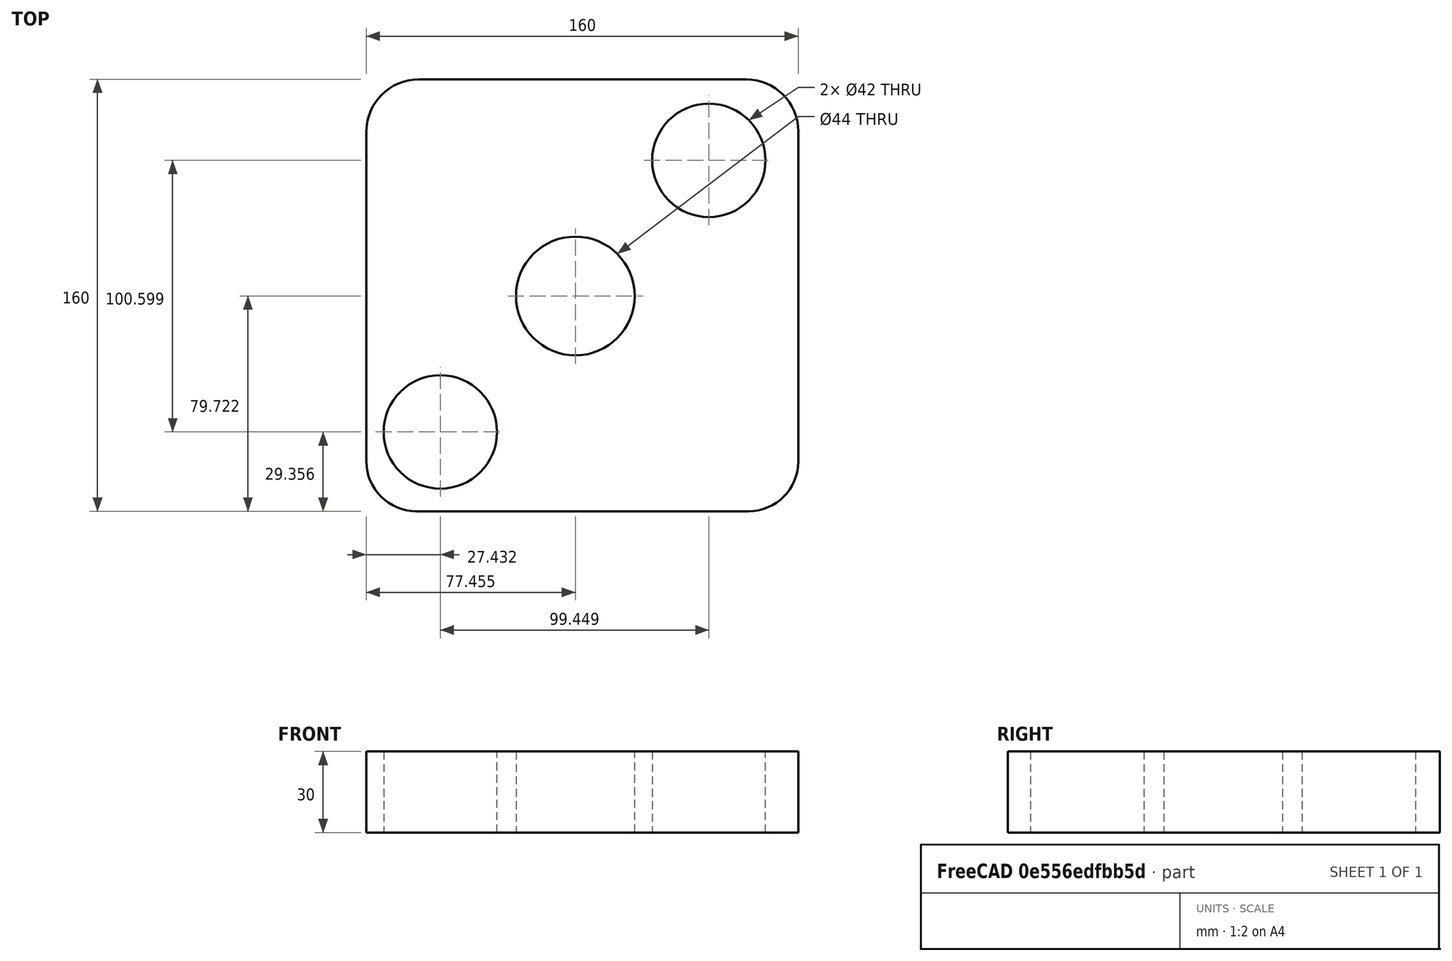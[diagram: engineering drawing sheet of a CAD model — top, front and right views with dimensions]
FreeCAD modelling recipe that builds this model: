
FCSTD DOCUMENT  (FreeCAD 0.18R16131 (Git))
Label: Momentum_Mold_Plate_1-3_160X160
License: All rights reserved
LicenseURL: http://en.wikipedia.org/wiki/All_rights_reserved
objects: Sketcher::SketchObject×1, PartDesign::Pad×1, PartDesign::Body×1
note: 4 computed .brp shape members not serialized (recipe doc carries the construction recipe); baked Part::Feature solids carry a one-line shape summary decoded from their .brp

FEATURE [Sketcher::SketchObject] Sketch
  MapMode = 5
  Support = -> [XY_Plane]
  sketch-geometry (11):
    g0: LineSegment StartX=-58.3579 StartY=-60.0631 StartZ=0 EndX=64.6457 EndY=-60.0631 EndZ=0
    g1: LineSegment StartX=83.0124 StartY=-41.6964 StartZ=0 EndX=83.0124 EndY=80.6112 EndZ=0
    g2: LineSegment StartX=63.6866 StartY=99.9369 StartZ=0 EndX=-57.4704 EndY=99.9369 EndZ=0
    g3: LineSegment StartX=-76.9876 StartY=80.4196 StartZ=0 EndX=-76.9876 EndY=-41.4333 EndZ=0
    g4: ArcOfCircle CenterX=-57.4704 CenterY=80.4196 CenterZ=0 NormalX=0 NormalY=0 NormalZ=1 AngleXU=0 Radius=19.5173 StartAngle=1.5708 EndAngle=3.14159
    g5: ArcOfCircle CenterX=63.6866 CenterY=80.6112 CenterZ=0 NormalX=0 NormalY=0 NormalZ=1 AngleXU=0 Radius=19.3258 StartAngle=0 EndAngle=1.5708
    g6: ArcOfCircle CenterX=64.6457 CenterY=-41.6964 CenterZ=0 NormalX=0 NormalY=0 NormalZ=1 AngleXU=0 Radius=18.3666 StartAngle=4.71239 EndAngle=6.28319
    g7: ArcOfCircle CenterX=-58.3579 CenterY=-41.4333 CenterZ=0 NormalX=0 NormalY=0 NormalZ=1 AngleXU=0 Radius=18.6298 StartAngle=3.14159 EndAngle=4.71239
    g8: Circle CenterX=-49.558 CenterY=-30.7045 CenterZ=0 NormalX=0 NormalY=0 NormalZ=1 AngleXU=0 Radius=21
    g9: Circle CenterX=49.8911 CenterY=69.8944 CenterZ=0 NormalX=0 NormalY=0 NormalZ=1 AngleXU=0 Radius=21
    g10: Circle CenterX=0.465053 CenterY=19.662 CenterZ=0 NormalX=0 NormalY=0 NormalZ=1 AngleXU=0 Radius=22
  constraints (15):
    c: Horizontal(g0)
    c: Horizontal(g2)
    c: Vertical(g1)
    c: Vertical(g3)
    c: Tangent(g2,g4) = -1.5708
    c: Tangent(g3,g4) = -1.5708
    c: Tangent(g2,g5) = -1.5708
    c: Tangent(g1,g5) = -1.5708
    c: Tangent(g1,g6) = -1.5708
    c: Tangent(g0,g6) = -1.5708
    c: Tangent(g0,g7) = -1.5708
    c: Tangent(g3,g7) = -1.5708
    c: Radius(g8) = 21
    c: Radius(g9) = 21
    c: Radius(g10) = 22
FEATURE [PartDesign::Pad] Pad
  Length = 30
  Length2 = 100
  Profile = -> Sketch
  Type = 0
FEATURE [PartDesign::Body] Body
  Group = -> [Sketch,Pad]
  Origin = -> Origin
  Tip = -> Pad
